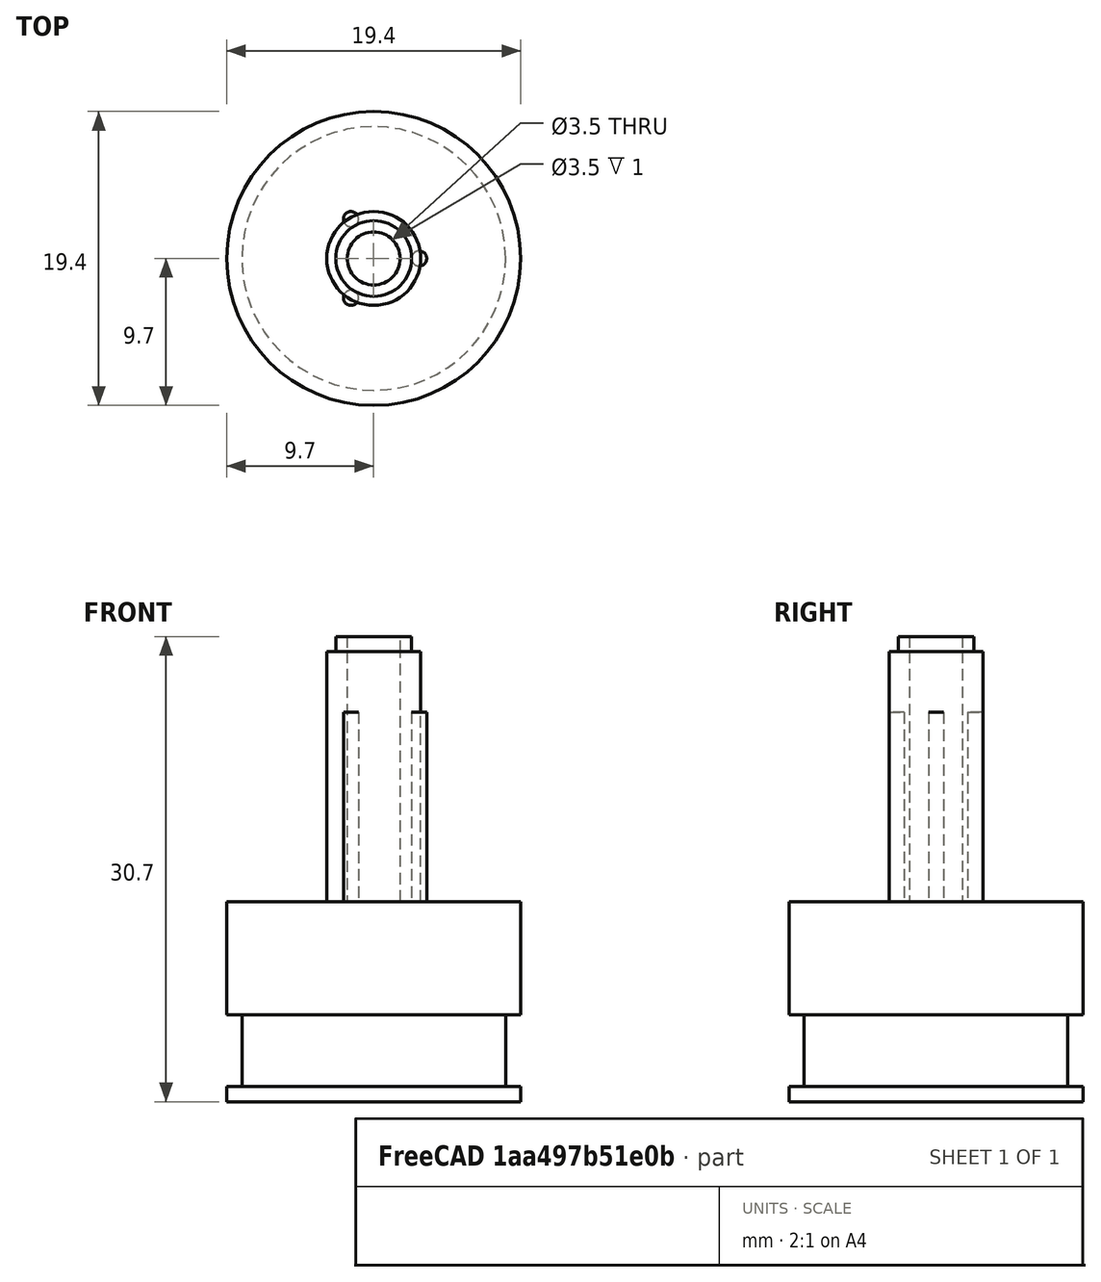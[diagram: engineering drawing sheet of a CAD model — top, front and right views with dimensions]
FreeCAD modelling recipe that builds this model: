
FCSTD DOCUMENT  (FreeCAD 0.20R29603 (Git))
Label: liebherr-freezer-door-post
License: All rights reserved
LicenseURL: http://en.wikipedia.org/wiki/All_rights_reserved
objects: Part::Cylinder×10, Part::Cut×2
note: 12 computed .brp shape members not serialized (recipe doc carries the construction recipe); baked Part::Feature solids carry a one-line shape summary decoded from their .brp

FEATURE [Part::Cylinder] Cylinder  label="Bottom (upper)"
  Angle = 360
  AttacherType = Attacher::AttachEngine3D
  FirstAngle = 0
  Height = 7.45
  Placement = pos=(0,0,5.75) rot=(0,0,1;0rad)
  Radius = 9.7
  SecondAngle = 0
FEATURE [Part::Cylinder] Cylinder001  label="Cable tie groove"
  Angle = 360
  AttacherType = Attacher::AttachEngine3D
  FirstAngle = 0
  Height = 4.75
  Placement = pos=(0,0,1) rot=(0,0,1;0rad)
  Radius = 8.7
  SecondAngle = 0
FEATURE [Part::Cylinder] Cylinder002  label="Bottom (lower)"
  Angle = 360
  AttacherType = Attacher::AttachEngine3D
  FirstAngle = 0
  Height = 1
  Radius = 9.7
  SecondAngle = 0
FEATURE [Part::Cylinder] Cylinder003  label="Top (outer 1)"
  Angle = 360
  AttacherType = Attacher::AttachEngine3D
  FirstAngle = 0
  Height = 16.5
  Placement = pos=(0,0,13.2) rot=(0,0,1;0rad)
  Radius = 3.1
  SecondAngle = 0
FEATURE [Part::Cylinder] Cylinder004  label="Top (outer 2)"
  Angle = 360
  AttacherType = Attacher::AttachEngine3D
  FirstAngle = 0
  Height = 1
  Placement = pos=(0,0,29.7) rot=(0,0,1;0rad)
  Radius = 2.5
  SecondAngle = 0
FEATURE [Part::Cylinder] Cylinder005  label="Top (inner 2)"
  Angle = 360
  AttacherType = Attacher::AttachEngine3D
  FirstAngle = 0
  Height = 1
  Placement = pos=(0,0,29.7) rot=(0,0,1;0rad)
  Radius = 1.75
  SecondAngle = 0
FEATURE [Part::Cylinder] Cylinder006  label="Ridge 0"
  Angle = 360
  AttacherType = Attacher::AttachEngine3D
  FirstAngle = 0
  Height = 12.5
  Placement = pos=(3,0,13.2) rot=(0,0,1;0rad)
  Radius = 0.5
  SecondAngle = 0
FEATURE [Part::Cylinder] Cylinder007  label="Top (inner 1)"
  Angle = 360
  AttacherType = Attacher::AttachEngine3D
  FirstAngle = 0
  Height = 16.5
  Placement = pos=(0,0,13.2) rot=(0,0,1;0rad)
  Radius = 1.75
  SecondAngle = 0
FEATURE [Part::Cut] Cut  label="Top (cut 1)"
  Base = -> Cylinder003
  Tool = -> Cylinder007
FEATURE [Part::Cut] Cut001  label="Top (cut 2)"
  Base = -> Cylinder004
  Tool = -> Cylinder005
FEATURE [Part::Cylinder] Cylinder008  label="Ridge 120"
  Angle = 360
  AttacherType = Attacher::AttachEngine3D
  FirstAngle = 0
  Height = 12.5
  Placement = pos=(-1.5,2.59808,13.2) rot=(0,0,1;2.0944rad)
  Radius = 0.5
  SecondAngle = 0
FEATURE [Part::Cylinder] Cylinder009  label="Ridge 240"
  Angle = 360
  AttacherType = Attacher::AttachEngine3D
  FirstAngle = 0
  Height = 12.5
  Placement = pos=(-1.5,-2.59808,13.2) rot=(0,0,1;4.18879rad)
  Radius = 0.5
  SecondAngle = 0
